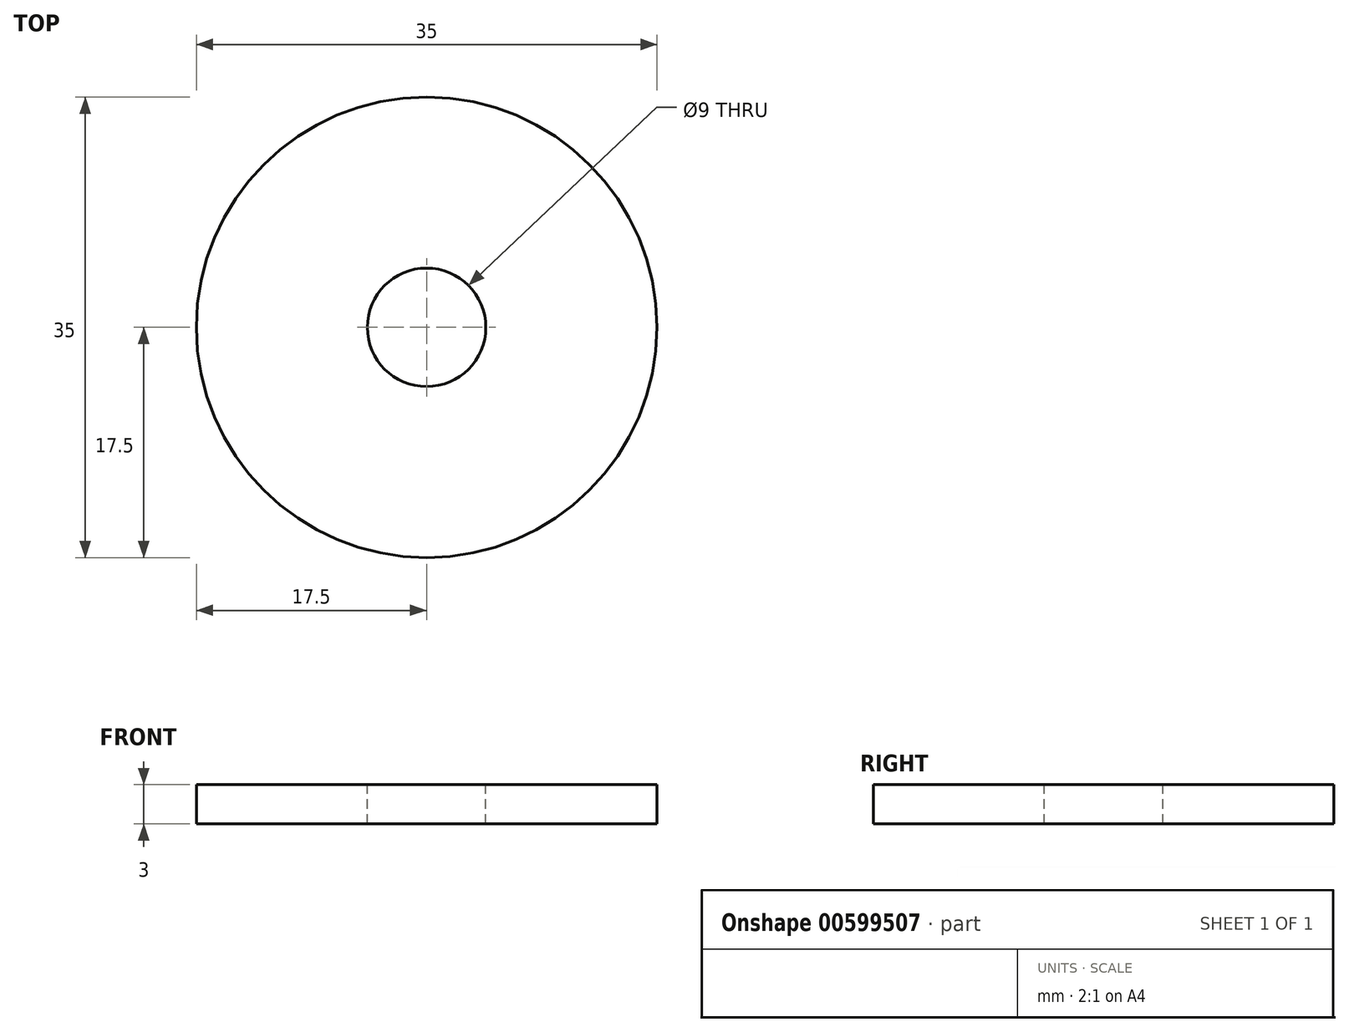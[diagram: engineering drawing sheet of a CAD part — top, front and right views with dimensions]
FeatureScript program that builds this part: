
annotation { "Feature Type Name" : "Feature", "Feature Type Description" : "" }
export const myFeature = defineFeature(function(context is Context, id is Id, definition is map)
    precondition{}
    {
        {
            var Q0;
            Q0=qCreatedBy(makeId("Front.planeOp"),FACE);
            var sketch = newSketch(context, id + "F0", { "sketchPlane" : qUnion([Q0])});
            skLineSegment(sketch, "E0", {"start": v(0, 3.38) * mm, "end": v(0, 0) * mm, "construction": true});
            skLineSegment(sketch, "E1", {"start": v(0, 0) * mm, "end": v(-17.5, 0) * mm, "construction": true});
            skLineSegment(sketch, "E2.bottom", {"start": v(-17.5, 0) * mm, "end": v(-4.5, 0) * mm});
            skLineSegment(sketch, "E2.top", {"start": v(-17.5, -3) * mm, "end": v(-4.5, -3) * mm});
            skLineSegment(sketch, "E2.left", {"start": v(-17.5, 0) * mm, "end": v(-17.5, -3) * mm});
            skLineSegment(sketch, "E2.right", {"start": v(-4.5, 0) * mm, "end": v(-4.5, -3) * mm});
            skSolve(sketch);
        }
        {
            var Q0;
            Q0 = qSketchRegion(id + "F0", true);
            var Q1;
            Q1=sQuery(id+"F0.wireOp",EDGE,"E0");
            revolve(context, id + "F1", {"entities" : qUnion([Q0]), "axis" : qUnion([Q1]), "revolveType" : RevolveType.FULL});
        }
    });
